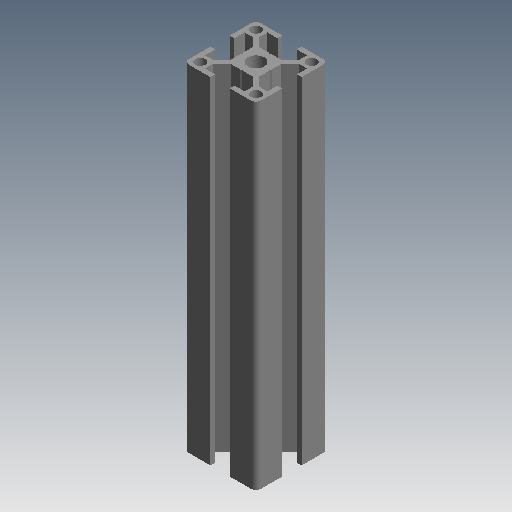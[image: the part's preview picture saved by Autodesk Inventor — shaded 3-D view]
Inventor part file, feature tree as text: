
AUTODESK INVENTOR PART (.ipt)
format: ipt  version: 2020 (Build 240168000, 168)  size: 209,920 bytes
history: native  units: mm (DEFAULTED — no unit token found)
features: other x21, sketch x3, hole x2, extrude x1, pattern_linear x1
ambient origin geometry x8: Origin, YZ Plane, XZ Plane, XY Plane, X Axis, Y Axis, Z Axis, Center Point
bodies: Solid1 (feature_tree)
feature tree (28):
  extrude  "Extrusion1"  Depth=140.0mm
  hole  "Hole1"  [1 undecoded]
  hole  "Hole2"  [1 undecoded]
  pattern_linear  "Rectangular Pattern1"  [2 undecoded]
  other  "C1_XY"
  other  "C1_YZ"
  other  "C1_ZX"
  other  "C1_X"
  other  "C1_Y"
  other  "C1_Z"
  other  "C1_Center"
  other  "to_frame_cap1_XY"
  other  "to_frame_cap1_YZ"
  other  "to_frame_cap1_ZX"
  other  "to_frame_cap1_X"
  other  "to_frame_cap1_Y"
  other  "to_frame_cap1_Z"
  other  "to_frame_cap1_Center"
  other  "to_frame_cap2_XY"
  other  "to_frame_cap2_YZ"
  other  "to_frame_cap2_ZX"
  other  "to_frame_cap2_X"
  other  "to_frame_cap2_Y"
  other  "to_frame_cap2_Z"
  other  "to_frame_cap2_Center"
  sketch  "Sketch_1"  dims[d0=140.0mm d1=0.0mm]
  sketch  "Sketch2"  dims[d2=6.8mm d3=6.0mm d4=4.0mm d5=2.0mm d6=90.0deg d7=140.0mm d8=0.0mm]
  sketch  "Sketch3"  dims[d9=4.2mm d10=6.0mm d11=4.0mm d12=2.0mm d13=90.0deg d14=140.0mm d15=0.0mm d16=20.0mm d18=23.2mm d19=20.0mm d21=23.2mm d22=0.0mm d23=0.0mm d24=0.0mm]
note: 4 required parameter values undecoded (feature->parameter linkage not recoverable at this tier; creation-order binding heuristic only, values carry confidence <= 0.55)
